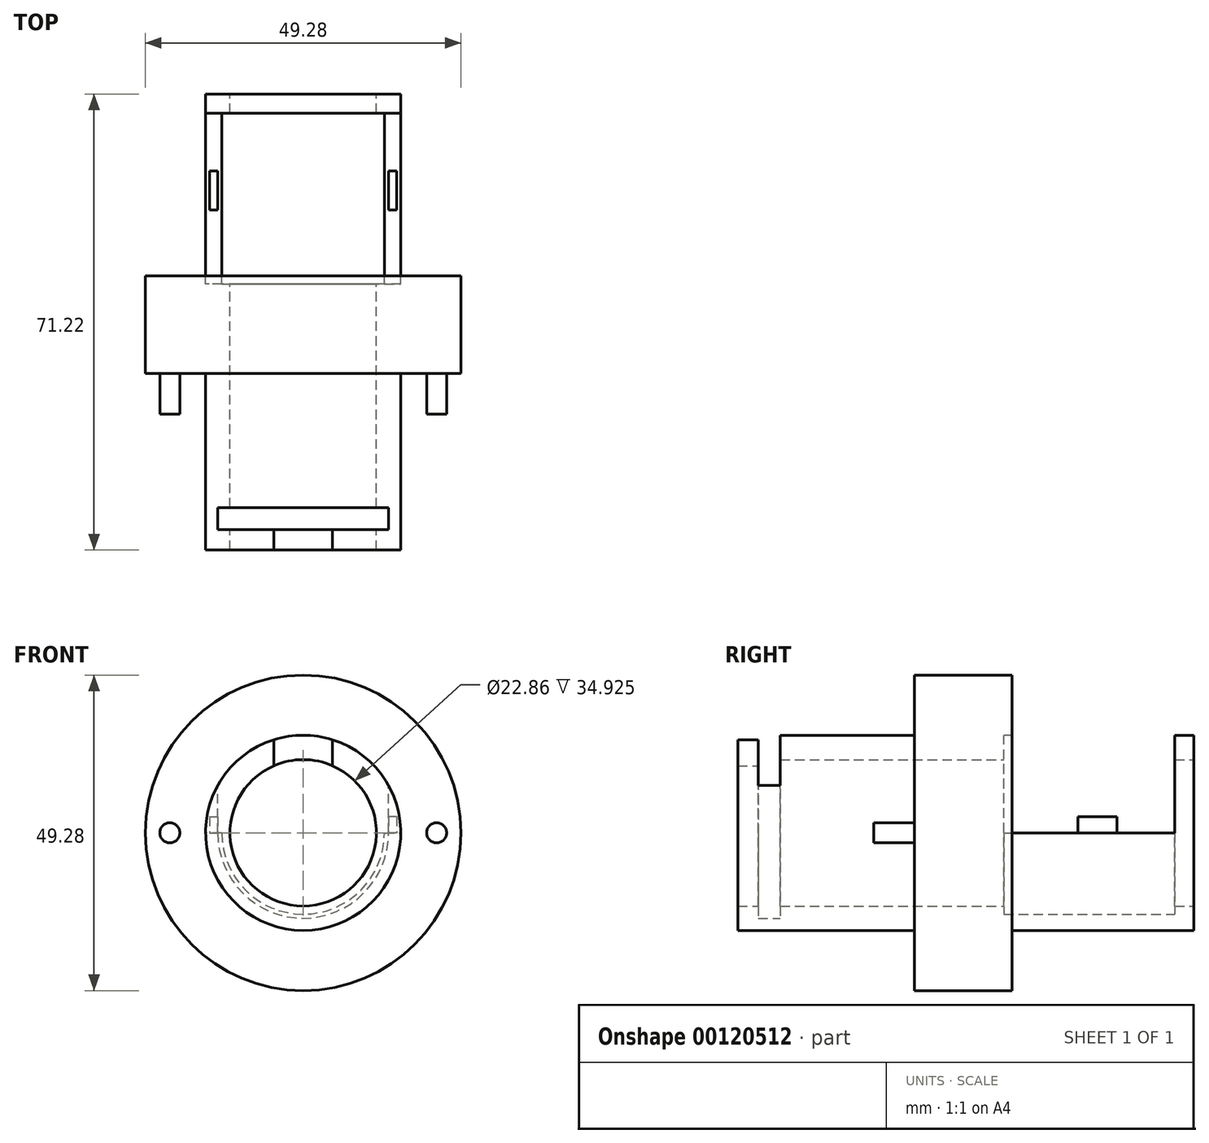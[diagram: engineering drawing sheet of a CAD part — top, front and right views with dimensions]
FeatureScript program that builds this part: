
annotation { "Feature Type Name" : "Feature", "Feature Type Description" : "" }
export const myFeature = defineFeature(function(context is Context, id is Id, definition is map)
    precondition{}
    {
        {
            var Q0;
            Q0=qCreatedBy(makeId("Front.planeOp"),FACE);
            var sketch = newSketch(context, id + "F0", { "sketchPlane" : qUnion([Q0])});
            skCircle(sketch, "E0", {"center": v(0, 0) * mm, "radius": 11.43 * mm});
            skCircle(sketch, "E1", {"center": v(0, 0) * mm, "radius": 15.24 * mm});
            skSolve(sketch);
        }
        {
            var Q0;
            Q0 = qSketchRegion(id + "F0", true);
            extrude(context, id + "F1", {"entities" : qUnion([Q0]), "depth" : 3 * mm});
        }
        {
            var Q0;
            Q0=makeQuery(id+"F1.opExtrude","CAP_FACE",FACE,{"disambiguationData":[OSD([sQuery(id+"F0.wireOp",EDGE,"E0"),sQuery(id+"F0.wireOp",EDGE,"E1")])],"isStart":false});
            var sketch = newSketch(context, id + "F2", { "sketchPlane" : qUnion([Q0])});
            skCircle(sketch, "E2", {"center": v(0, 0) * mm, "radius": 12.7 * mm});
            skCircle(sketch, "E3", {"center": v(0, 0) * mm, "radius": 15.24 * mm});
            skLineSegment(sketch, "E4", {"start": v(-12.7, 0) * mm, "end": v(-12.7, 8.42) * mm});
            skLineSegment(sketch, "E5", {"start": v(12.7, 0) * mm, "end": v(12.7, 8.42) * mm});
            skLineSegment(sketch, "E6", {"start": v(-12.7, 0) * mm, "end": v(-15.24, 0) * mm});
            skLineSegment(sketch, "E7", {"start": v(12.7, 0) * mm, "end": v(15.24, 0) * mm});
            skSolve(sketch);
        }
        {
            var Q0;
            {var subQ0=sQuery(id+"F2.wireOp",EDGE,"E6");Q0=makeQuery(id+"F2.imprint","IMPRINT",FACE,{"disambiguationData":[TD([[makeQuery(id+"F2.imprint","IMPRINT",EDGE,{"derivedFrom":subQ0}),1.0]])]});}
            extrude(context, id + "F3", {"entities" : qUnion([Q0]), "operationType" : NewBodyOperationType.ADD, "depth" : 26.67 * mm});
        }
        {
            var Q0;
            Q0=makeQuery(id+"F3.opExtrude","CAP_FACE",FACE,{"disambiguationData":[OSD([sQuery(id+"F2.wireOp",EDGE,"E2"),sQuery(id+"F2.wireOp",EDGE,"E3"),sQuery(id+"F2.wireOp",EDGE,"E4"),sQuery(id+"F2.wireOp",EDGE,"E5")])],"isStart":false});
            var sketch = newSketch(context, id + "F4", { "sketchPlane" : qUnion([Q0])});
            skCircle(sketch, "E8", {"center": v(0, 0) * mm, "radius": 11.43 * mm});
            skCircle(sketch, "E9", {"center": v(0, 0) * mm, "radius": 15.24 * mm});
            skSolve(sketch);
        }
        {
            var Q0;
            Q0 = qSketchRegion(id + "F4", true);
            extrude(context, id + "F5", {"entities" : qUnion([Q0]), "operationType" : NewBodyOperationType.ADD, "depth" : 2.54 * mm});
        }
        {
            var Q0;
            Q0=qCreatedBy(makeId("Top.planeOp"),FACE);
            var sketch = newSketch(context, id + "F6", { "sketchPlane" : qUnion([Q0])});
            skLineSegment(sketch, "E10.bottom", {"start": v(-13.33, -68.02) * mm, "end": v(13.34, -68.02) * mm});
            skLineSegment(sketch, "E10.top", {"start": v(-13.33, -64.72) * mm, "end": v(13.34, -64.72) * mm});
            skLineSegment(sketch, "E10.left", {"start": v(-13.33, -68.02) * mm, "end": v(-13.33, -64.72) * mm});
            skLineSegment(sketch, "E10.right", {"start": v(13.34, -68.02) * mm, "end": v(13.34, -64.72) * mm});
            skLineSegment(sketch, "E11.bottom", {"start": v(-4.57, -74.37) * mm, "end": v(4.57, -74.37) * mm});
            skLineSegment(sketch, "E11.top", {"start": v(-4.57, -68.02) * mm, "end": v(4.57, -68.02) * mm});
            skLineSegment(sketch, "E11.left", {"start": v(-4.57, -74.37) * mm, "end": v(-4.57, -68.02) * mm});
            skLineSegment(sketch, "E11.right", {"start": v(4.57, -74.37) * mm, "end": v(4.57, -68.02) * mm});
            skSolve(sketch);
        }
        {
            var Q0;
            Q0 = qSketchRegion(id + "F6", true);
            extrude(context, id + "F7", {"entities" : qUnion([Q0]), "operationType" : NewBodyOperationType.REMOVE, "depth" : 28.57 * mm});
        }
        {
            var Q0;
            Q0=makeQuery(id+"F3.opExtrude","SWEPT_FACE",FACE,{"disambiguationData":[OSD([sQuery(id+"F2.wireOp",EDGE,"E7")])]});
            var sketch = newSketch(context, id + "F8", { "sketchPlane" : qUnion([Q0])});
            skLineSegment(sketch, "E12.bottom", {"start": v(14.6, -18.11) * mm, "end": v(13.34, -18.11) * mm});
            skLineSegment(sketch, "E12.top", {"start": v(14.6, -12.01) * mm, "end": v(13.33, -12.01) * mm});
            skLineSegment(sketch, "E12.left", {"start": v(14.6, -18.11) * mm, "end": v(14.6, -12.01) * mm});
            skLineSegment(sketch, "E12.right", {"start": v(13.33, -18.11) * mm, "end": v(13.33, -12.01) * mm});
            skLineSegment(sketch, "E13.MirrorCS", {"start": v(-14.6, -18.11) * mm, "end": v(-14.6, -12.01) * mm});
            skLineSegment(sketch, "E14.MirrorCS", {"start": v(-13.33, -18.11) * mm, "end": v(-13.33, -12.01) * mm});
            skLineSegment(sketch, "E15.MirrorCS", {"start": v(-14.6, -12.01) * mm, "end": v(-13.33, -12.01) * mm});
            skLineSegment(sketch, "E16.MirrorCS", {"start": v(-14.6, -18.11) * mm, "end": v(-13.34, -18.11) * mm});
            skSolve(sketch);
        }
        {
            var Q0;
            Q0 = qSketchRegion(id + "F8", true);
            extrude(context, id + "F9", {"entities" : qUnion([Q0]), "operationType" : NewBodyOperationType.ADD, "depth" : 2.54 * mm});
        }
        {
            var Q0;
            Q0=makeQuery(id+"F5.opExtrude","CAP_FACE",FACE,{"disambiguationData":[OSD([sQuery(id+"F4.wireOp",EDGE,"E8"),sQuery(id+"F4.wireOp",EDGE,"E9")])],"isStart":false});
            var sketch = newSketch(context, id + "F10", { "sketchPlane" : qUnion([Q0])});
            skCircle(sketch, "E17", {"center": v(0, 0) * mm, "radius": 24.64 * mm});
            skCircle(sketch, "E18", {"center": v(0, 0) * mm, "radius": 15.24 * mm});
            skSolve(sketch);
        }
        {
            var Q0;
            Q0=makeQuery(id+"F10.imprint","IMPRINT",FACE,{"disambiguationData":[TD([[makeQuery(id+"F10.imprint","IMPRINT",EDGE,{"derivedFrom":sQuery(id+"F10.wireOp",EDGE,"E17")}),1.0]])]});
            extrude(context, id + "F11", {"entities" : qUnion([Q0]), "operationType" : NewBodyOperationType.ADD, "oppositeDirection" : true, "depth" : 3.8 * mm});
        }
        {
            var Q0;
            Q0=makeQuery(id+"F11.boolean.opBoolean","MERGE",FACE,{"derivedFrom":[makeQuery(id+"F5.opExtrude","CAP_FACE",FACE,{"disambiguationData":[OSD([sQuery(id+"F4.wireOp",EDGE,"E8"),sQuery(id+"F4.wireOp",EDGE,"E9")])],"isStart":false}),makeQuery(id+"F11.opExtrude","CAP_FACE",FACE,{"disambiguationData":[OSD([sQuery(id+"F10.wireOp",EDGE,"E17"),sQuery(id+"F10.wireOp",EDGE,"E18")])],"isStart":true})]});
            extrude(context, id + "F12", {"entities" : qUnion([Q0]), "operationType" : NewBodyOperationType.ADD, "depth" : 11.43 * mm});
        }
        {
            var Q0;
            Q0=makeQuery(id+"F12.opExtrude","CAP_FACE",FACE,{"disambiguationData":[OSD([sQuery(id+"F4.wireOp",EDGE,"E8"),sQuery(id+"F4.wireOp",EDGE,"E9"),sQuery(id+"F10.wireOp",EDGE,"E17"),sQuery(id+"F10.wireOp",EDGE,"E18")])],"isStart":false});
            var sketch = newSketch(context, id + "F13", { "sketchPlane" : qUnion([Q0])});
            skCircle(sketch, "E19", {"center": v(0, 0) * mm, "radius": 11.43 * mm});
            skCircle(sketch, "E20", {"center": v(0, 0) * mm, "radius": 15.24 * mm});
            skSolve(sketch);
        }
        {
            var Q0;
            Q0 = qSketchRegion(id + "F13", true);
            extrude(context, id + "F14", {"entities" : qUnion([Q0]), "operationType" : NewBodyOperationType.ADD, "depth" : 20.95 * mm});
        }
        {
            var Q0;
            Q0=makeQuery(id+"F14.opExtrude","CAP_FACE",FACE,{"disambiguationData":[OSD([sQuery(id+"F13.wireOp",EDGE,"E19"),sQuery(id+"F13.wireOp",EDGE,"E20")])],"isStart":false});
            var sketch = newSketch(context, id + "F15", { "sketchPlane" : qUnion([Q0])});
            skCircle(sketch, "E21", {"center": v(0, 0) * mm, "radius": 13.34 * mm});
            skCircle(sketch, "E22", {"center": v(0, 0) * mm, "radius": 15.24 * mm});
            skLineSegment(sketch, "E23", {"start": v(13.34, 0) * mm, "end": v(13.34, 7.38) * mm});
            skLineSegment(sketch, "E24.MirrorCS", {"start": v(-13.34, 0) * mm, "end": v(-13.34, 7.38) * mm});
            skSolve(sketch);
        }
        {
            var Q0;
            {var subQ0=sQuery(id+"F15.wireOp",EDGE,"E23");Q0=makeQuery(id+"F15.imprint","IMPRINT",FACE,{"disambiguationData":[TD([[makeQuery(id+"F15.imprint","IMPRINT",EDGE,{"derivedFrom":subQ0}),-1.0]])]});}
            extrude(context, id + "F16", {"entities" : qUnion([Q0]), "operationType" : NewBodyOperationType.ADD, "depth" : 3.45 * mm});
        }
        {
            var Q0;
            Q0=makeQuery(id+"F16.opExtrude","CAP_FACE",FACE,{"disambiguationData":[OSD([sQuery(id+"F15.wireOp",EDGE,"E21"),sQuery(id+"F15.wireOp",EDGE,"E22"),sQuery(id+"F15.wireOp",EDGE,"E23"),sQuery(id+"F15.wireOp",EDGE,"E24.MirrorCS")])],"isStart":false});
            var sketch = newSketch(context, id + "F17", { "sketchPlane" : qUnion([Q0])});
            skCircle(sketch, "E25", {"center": v(0, 0) * mm, "radius": 11.43 * mm});
            skCircle(sketch, "E26", {"center": v(0, 0) * mm, "radius": 15.24 * mm});
            skSolve(sketch);
        }
        {
            var Q0;
            Q0 = qSketchRegion(id + "F17", true);
            extrude(context, id + "F18", {"entities" : qUnion([Q0]), "operationType" : NewBodyOperationType.ADD, "depth" : 3.17 * mm});
        }
        {
            var Q0;
            Q0 = qSketchRegion(id + "F6", true);
            extrude(context, id + "F19", {"entities" : qUnion([Q0]), "operationType" : NewBodyOperationType.REMOVE, "depth" : 25.4 * mm});
        }
        {
            var Q0;
            Q0=makeQuery(id+"F12.opExtrude","CAP_FACE",FACE,{"disambiguationData":[OSD([sQuery(id+"F4.wireOp",EDGE,"E8"),sQuery(id+"F4.wireOp",EDGE,"E9"),sQuery(id+"F10.wireOp",EDGE,"E17"),sQuery(id+"F10.wireOp",EDGE,"E18")])],"isStart":false});
            var sketch = newSketch(context, id + "F20", { "sketchPlane" : qUnion([Q0])});
            skCircle(sketch, "E27", {"center": v(20.83, 0) * mm, "radius": 1.56 * mm});
            skCircle(sketch, "E28.MirrorC", {"center": v(-20.83, 0) * mm, "radius": 1.56 * mm});
            skSolve(sketch);
        }
        {
            var Q0;
            Q0 = qSketchRegion(id + "F20", true);
            extrude(context, id + "F21", {"entities" : qUnion([Q0]), "operationType" : NewBodyOperationType.ADD, "depth" : 6.35 * mm});
        }
    });
